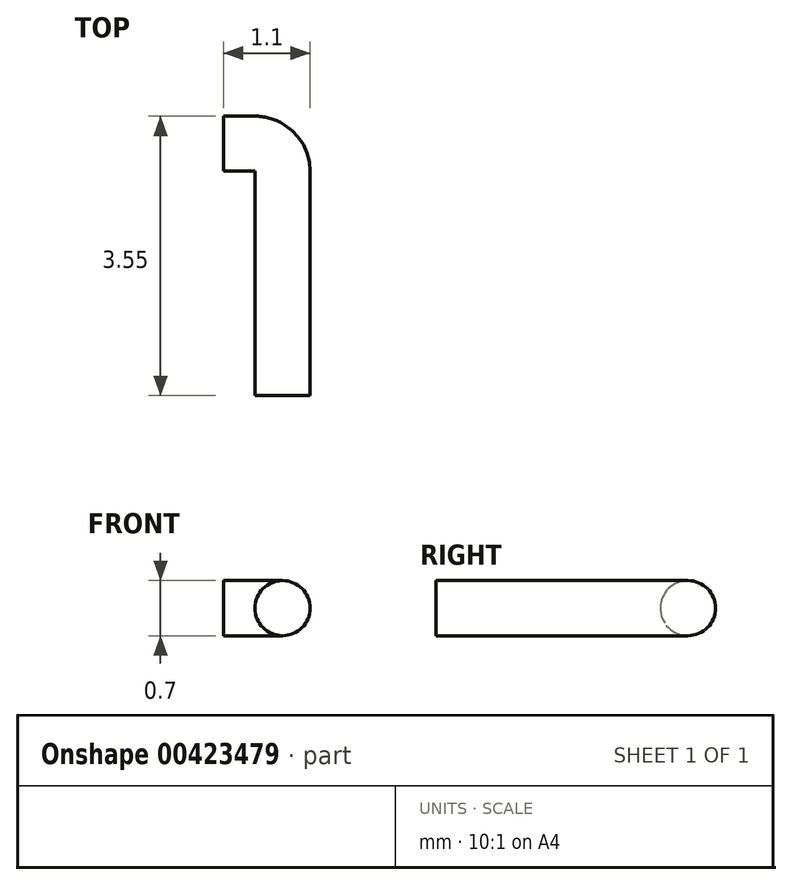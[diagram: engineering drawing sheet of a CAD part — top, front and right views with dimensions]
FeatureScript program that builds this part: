
annotation { "Feature Type Name" : "Feature", "Feature Type Description" : "" }
export const myFeature = defineFeature(function(context is Context, id is Id, definition is map)
    precondition{}
    {
        {
            var Q0;
            Q0=qCreatedBy(makeId("Top.planeOp"),FACE);
            var sketch = newSketch(context, id + "F0", { "sketchPlane" : qUnion([Q0])});
            skLineSegment(sketch, "E0", {"start": v(0, 0) * mm, "end": v(0.4, 0) * mm});
            skLineSegment(sketch, "E1", {"start": v(0.75, -0.35) * mm, "end": v(0.75, -3.2) * mm});
            skPoint(sketch, "E2.visualSharp", {"position": v(0.75, 0) * mm});
            skArc(sketch, "E2.filletArc", {"start": v(0.75, -0.35) * mm, "mid": v(0.65, -0.1) * mm, "end": v(0.4, 0) * mm});
            skSolve(sketch);
        }
        {
            var Q0;
            Q0=qCreatedBy(makeId("Right.planeOp"),FACE);
            var sketch = newSketch(context, id + "F1", { "sketchPlane" : qUnion([Q0])});
            skCircle(sketch, "E3", {"center": v(0, 0) * mm, "radius": 0.35 * mm});
            skSolve(sketch);
        }
        {
            var Q0;
            Q0=makeQuery(id+"F1.imprint","IMPRINT",FACE,{"disambiguationData":[TD([[makeQuery(id+"F1.imprint","IMPRINT",EDGE,{"derivedFrom":sQuery(id+"F1.wireOp",EDGE,"E3")}),1.0]])]});
            var Q1;
            Q1=sQuery(id+"F0.wireOp",EDGE,"E0");
            var Q2;
            Q2=sQuery(id+"F0.wireOp",EDGE,"E1");
            var Q3;
            Q3=sQuery(id+"F0.wireOp",EDGE,"E2.filletArc");
            sweep(context, id + "F2", {"profiles" : qUnion([Q0]), "path" : qUnion([Q1, Q2, Q3])});
        }
    });
